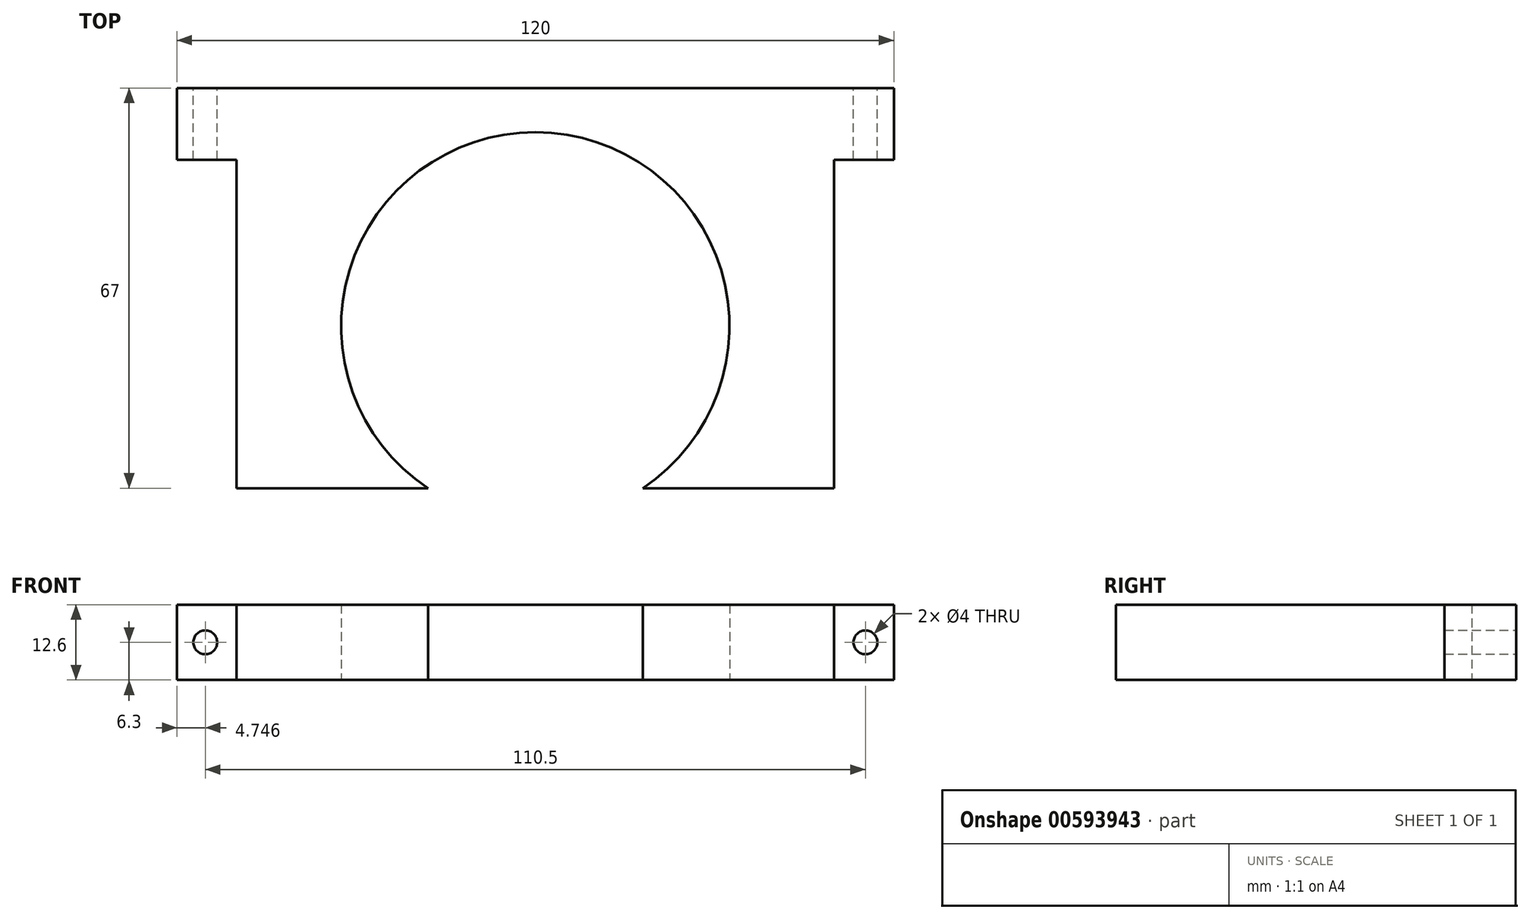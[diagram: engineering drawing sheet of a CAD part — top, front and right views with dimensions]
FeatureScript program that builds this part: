
annotation { "Feature Type Name" : "Feature", "Feature Type Description" : "" }
export const myFeature = defineFeature(function(context is Context, id is Id, definition is map)
    precondition{}
    {
        {
            var Q0;
            Q0=qCreatedBy(makeId("Top.planeOp"),FACE);
            var sketch = newSketch(context, id + "F0", { "sketchPlane" : qUnion([Q0])});
            skLineSegment(sketch, "E0.bottom", {"start": v(-41.07, 32.19) * mm, "end": v(78.93, 32.19) * mm});
            skCircle(sketch, "E1", {"center": v(18.93, -7.73) * mm, "radius": 32.5 * mm});
            skPoint(sketch, "E1.centerSnap1", {"position": v(18.93, 32.19) * mm});
            skLineSegment(sketch, "E2", {"start": v(78.93, 32.19) * mm, "end": v(78.93, -34.81) * mm});
            skLineSegment(sketch, "E3", {"start": v(-41.07, 32.19) * mm, "end": v(-41.07, -34.81) * mm});
            skCircle(sketch, "E4", {"center": v(18.93, -7.73) * mm, "radius": 42.5 * mm});
            skLineSegment(sketch, "E5", {"start": v(-41.07, -34.81) * mm, "end": v(-19.98, -34.81) * mm});
            skLineSegment(sketch, "E6", {"start": v(78.93, -34.81) * mm, "end": v(-19.98, -34.81) * mm});
            skPoint(sketch, "E7.visualSharp", {"position": v(-41.07, -34.81) * mm});
            skPoint(sketch, "E8.visualSharp", {"position": v(77.14, -34.81) * mm});
            skLineSegment(sketch, "E8.filletArc", {"start": v(78.93, -34.81) * mm, "end": v(78.93, -34.81) * mm});
            skLineSegment(sketch, "E9", {"start": v(-41.07, 20.19) * mm, "end": v(78.93, 20.19) * mm});
            skLineSegment(sketch, "E10", {"start": v(-31.07, 20.19) * mm, "end": v(-31.07, -34.81) * mm});
            skLineSegment(sketch, "E11", {"start": v(68.93, 20.19) * mm, "end": v(68.93, -37.23) * mm});
            skSolve(sketch);
        }
        {
            var Q0;
            Q0=makeQuery(id+"F0.imprint","IMPRINT",FACE,{"disambiguationData":[TD([[makeQuery(id+"F0.imprint","IMPRINT",EDGE,{"derivedFrom":sQuery(id+"F0.wireOp",EDGE,"E0.bottom")}),-1.0]])]});
            var Q1;
            {var subQ0=sQuery(id+"F0.wireOp",EDGE,"E4");var subQ1=sQuery(id+"F0.wireOp",EDGE,"E0.bottom");var subQ2=makeQuery(id+"F0.imprint","INTERSECT",VERTEX,{"disambiguationData":[OD(0.0)],"derivedFrom":[subQ1,subQ0]});Q1=makeQuery(id+"F0.imprint","IMPRINT",FACE,{"disambiguationData":[TD([[makeQuery(id+"F0.imprint","IMPRINT",EDGE,{"disambiguationData":[TD([[subQ2,-1.0]])],"derivedFrom":subQ1}),-1.0]])]});}
            var Q2;
            {var subQ1=sQuery(id+"F0.wireOp",EDGE,"09996e16-629e-4b57-9f6e-60e7eec62230.filletArc");Q2=makeQuery(id+"F0.imprint","IMPRINT",FACE,{"disambiguationData":[TD([[makeQuery(id+"F0.imprint","IMPRINT",EDGE,{"derivedFrom":subQ1}),1.0]])]});}
            var Q3;
            {var subQ1=sQuery(id+"F0.wireOp",EDGE,"80cf1b9d-a62e-4cef-96d0-c6d76e58feb5.filletArc");Q3=makeQuery(id+"F0.imprint","IMPRINT",FACE,{"disambiguationData":[TD([[makeQuery(id+"F0.imprint","IMPRINT",EDGE,{"derivedFrom":subQ1}),1.0]])]});}
            var Q4;
            {var subQ2=sQuery(id+"F0.wireOp",EDGE,"KSQB4hhD-aKC2-SD4m-8226-d75hPtoGRsX4.bottom");var subQ6=sQuery(id+"F0.wireOp",EDGE,"E1");var subQ7=makeQuery(id+"F0.imprint","INTERSECT",VERTEX,{"disambiguationData":[OD(0.0)],"derivedFrom":[subQ6,subQ2]});Q4=makeQuery(id+"F0.imprint","IMPRINT",FACE,{"disambiguationData":[TD([[makeQuery(id+"F0.imprint","IMPRINT",EDGE,{"disambiguationData":[TD([[subQ7,-1.0]])],"derivedFrom":subQ6}),-1.0]])]});}
            var Q5;
            {var subQ0=sQuery(id+"F0.wireOp",EDGE,"E9");var subQ1=sQuery(id+"F0.wireOp",EDGE,"E1");var subQ2=makeQuery(id+"F0.imprint","INTERSECT",VERTEX,{"disambiguationData":[OD(0.0)],"derivedFrom":[subQ1,subQ0]});Q5=makeQuery(id+"F0.imprint","IMPRINT",FACE,{"disambiguationData":[TD([[makeQuery(id+"F0.imprint","IMPRINT",EDGE,{"disambiguationData":[TD([[subQ2,1.0]])],"derivedFrom":subQ1}),-1.0]])]});}
            var Q6;
            {var subQ5=sQuery(id+"F0.wireOp",EDGE,"E11");Q6=makeQuery(id+"F0.imprint","IMPRINT",FACE,{"disambiguationData":[TD([[makeQuery(id+"F0.imprint","IMPRINT",EDGE,{"derivedFrom":subQ5}),-1.0]])]});}
            var Q7;
            {var subQ5=sQuery(id+"F0.wireOp",EDGE,"E10");Q7=makeQuery(id+"F0.imprint","IMPRINT",FACE,{"disambiguationData":[TD([[makeQuery(id+"F0.imprint","IMPRINT",EDGE,{"derivedFrom":subQ5}),1.0]])]});}
            var Q8;
            {var subQ0=sQuery(id+"F0.wireOp",EDGE,"E9");var subQ1=sQuery(id+"F0.wireOp",EDGE,"E1");var subQ2=makeQuery(id+"F0.imprint","INTERSECT",VERTEX,{"disambiguationData":[OD(0.0)],"derivedFrom":[subQ1,subQ0]});Q8=makeQuery(id+"F0.imprint","IMPRINT",FACE,{"disambiguationData":[TD([[makeQuery(id+"F0.imprint","IMPRINT",EDGE,{"disambiguationData":[TD([[subQ2,-1.0]])],"derivedFrom":subQ1}),-1.0]])]});}
            var Q9;
            {var subQ0=sQuery(id+"F0.wireOp",EDGE,"E9");var subQ1=sQuery(id+"F0.wireOp",EDGE,"E1");var subQ2=makeQuery(id+"F0.imprint","INTERSECT",VERTEX,{"disambiguationData":[OD(1.0)],"derivedFrom":[subQ1,subQ0]});Q9=makeQuery(id+"F0.imprint","IMPRINT",FACE,{"disambiguationData":[TD([[makeQuery(id+"F0.imprint","IMPRINT",EDGE,{"disambiguationData":[TD([[subQ2,1.0]])],"derivedFrom":subQ1}),-1.0]])]});}
            var Q10;
            {var subQ0=sQuery(id+"F0.wireOp",EDGE,"E6");var subQ1=sQuery(id+"F0.wireOp",EDGE,"E1");var subQ2=makeQuery(id+"F0.imprint","INTERSECT",VERTEX,{"disambiguationData":[OD(0.0)],"derivedFrom":[subQ1,subQ0]});Q10=makeQuery(id+"F0.imprint","IMPRINT",FACE,{"disambiguationData":[TD([[makeQuery(id+"F0.imprint","IMPRINT",EDGE,{"disambiguationData":[TD([[subQ2,-1.0]])],"derivedFrom":subQ1}),-1.0]])]});}
            extrude(context, id + "F1", {"entities" : qUnion([Q0, Q1, Q2, Q3, Q4, Q5, Q6, Q7, Q8, Q9, Q10]), "depth" : 12.6 * mm, "offsetDistance" : 25 * mm});
        }
        {
            var Q0;
            Q0=makeQuery(id+"F1.opExtrude","SWEPT_FACE",FACE,{"disambiguationData":[OSD([sQuery(id+"F0.wireOp",EDGE,"E0.bottom")])]});
            var sketch = newSketch(context, id + "F2", { "sketchPlane" : qUnion([Q0])});
            skCircle(sketch, "E12", {"center": v(-74.18, 6.3) * mm, "radius": 2 * mm});
            skPoint(sketch, "E12.centerSnap0", {"position": v(-78.93, 6.3) * mm});
            skCircle(sketch, "E13.1.0.1", {"center": v(36.32, 6.3) * mm, "radius": 2 * mm});
            skSolve(sketch);
        }
        {
            var Q0;
            Q0=makeQuery(id+"F2.imprint","IMPRINT",FACE,{"disambiguationData":[TD([[makeQuery(id+"F2.imprint","IMPRINT",EDGE,{"derivedFrom":sQuery(id+"F2.wireOp",EDGE,"E12")}),1.0]])]});
            var Q1;
            Q1=makeQuery(id+"F2.imprint","IMPRINT",FACE,{"disambiguationData":[TD([[makeQuery(id+"F2.imprint","IMPRINT",EDGE,{"derivedFrom":sQuery(id+"F2.wireOp",EDGE,"E13.1.0.1")}),1.0]])]});
            extrude(context, id + "F3", {"entities" : qUnion([Q0, Q1]), "operationType" : NewBodyOperationType.REMOVE, "endBound" : BoundingType.THROUGH_ALL, "oppositeDirection" : true, "depth" : 85 * mm, "offsetDistance" : 25 * mm});
        }
    });
